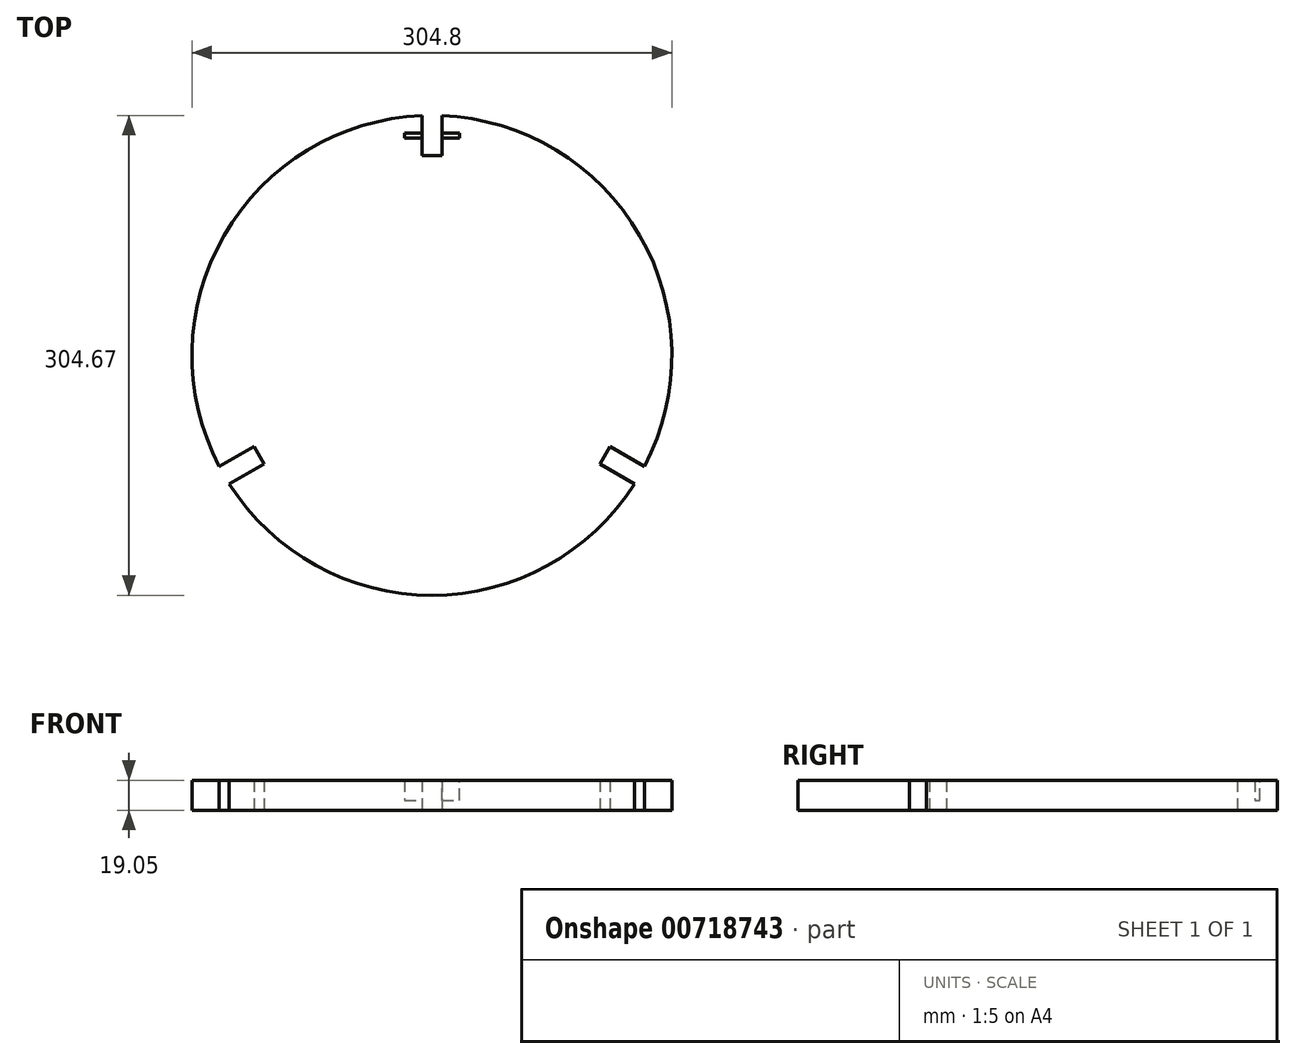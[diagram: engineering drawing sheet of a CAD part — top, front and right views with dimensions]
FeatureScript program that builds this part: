
annotation { "Feature Type Name" : "Feature", "Feature Type Description" : "" }
export const myFeature = defineFeature(function(context is Context, id is Id, definition is map)
    precondition{}
    {
        {
            var Q0;
            Q0=qCreatedBy(makeId("Top.planeOp"),FACE);
            var sketch = newSketch(context, id + "F0", { "sketchPlane" : qUnion([Q0])});
            skCircle(sketch, "E0", {"center": v(0, 0) * mm, "radius": 152.4 * mm});
            skLineSegment(sketch, "E1", {"start": v(0, 0) * mm, "end": v(0, 152.4) * mm, "construction": true});
            skLineSegment(sketch, "E2", {"start": v(0, 0) * mm, "end": v(131.98, -76.2) * mm, "construction": true});
            skLineSegment(sketch, "E3", {"start": v(0, 0) * mm, "end": v(-131.98, -76.2) * mm, "construction": true});
            skLineSegment(sketch, "E4", {"start": v(-6.35, 152.27) * mm, "end": v(-6.35, 126.87) * mm});
            skLineSegment(sketch, "E5", {"start": v(-6.35, 126.87) * mm, "end": v(6.35, 126.87) * mm});
            skLineSegment(sketch, "E6", {"start": v(6.35, 126.87) * mm, "end": v(6.35, 152.27) * mm});
            skLineSegment(sketch, "E7.1.0", {"start": v(-128.7, -81.63) * mm, "end": v(-106.7, -68.93) * mm});
            skLineSegment(sketch, "E7.1.1", {"start": v(-106.7, -68.93) * mm, "end": v(-113.05, -57.93) * mm});
            skLineSegment(sketch, "E7.1.2", {"start": v(-113.05, -57.93) * mm, "end": v(-135.04, -70.63) * mm});
            skLineSegment(sketch, "E7.2.0", {"start": v(135.04, -70.63) * mm, "end": v(113.05, -57.93) * mm});
            skLineSegment(sketch, "E7.2.1", {"start": v(113.05, -57.93) * mm, "end": v(106.7, -68.93) * mm});
            skLineSegment(sketch, "E7.2.2", {"start": v(106.7, -68.93) * mm, "end": v(128.7, -81.63) * mm});
            skSolve(sketch);
        }
        {
            var Q0;
            {var subQ0=sQuery(id+"F0.wireOp",EDGE,"E4");Q0=makeQuery(id+"F0.imprint","IMPRINT",FACE,{"disambiguationData":[TD([[makeQuery(id+"F0.imprint","IMPRINT",EDGE,{"derivedFrom":subQ0}),-1.0]])]});}
            extrude(context, id + "F1", {"entities" : qUnion([Q0]), "depth" : 19.05 * mm, "offsetDistance" : 25.4 * mm});
        }
        {
            var Q0;
            Q0=qCreatedBy(makeId("Right.planeOp"),FACE);
            var sketch = newSketch(context, id + "F2", { "sketchPlane" : qUnion([Q0])});
            skLineSegment(sketch, "E8.0.1", {"start": v(126.87, 0) * mm, "end": v(126.87, 19.05) * mm});
            skLineSegment(sketch, "E8.0.3", {"start": v(126.87, 19.05) * mm, "end": v(126.87, 0) * mm, "construction": true});
            skLineSegment(sketch, "E9.0", {"start": v(152.27, 19.05) * mm, "end": v(-70.63, 19.05) * mm, "construction": true});
            skLineSegment(sketch, "E10", {"start": v(137.98, 19.05) * mm, "end": v(137.98, 6.35) * mm});
            skLineSegment(sketch, "E11", {"start": v(137.98, 6.35) * mm, "end": v(141.16, 6.35) * mm});
            skLineSegment(sketch, "E12", {"start": v(141.16, 6.35) * mm, "end": v(141.16, 19.05) * mm});
            skLineSegment(sketch, "E13", {"start": v(137.98, 19.05) * mm, "end": v(141.16, 19.05) * mm});
            skLineSegment(sketch, "E14", {"start": v(139.57, 19.05) * mm, "end": v(139.57, 6.35) * mm, "construction": true});
            skLineSegment(sketch, "E15.0", {"start": v(152.27, 0) * mm, "end": v(-70.63, 0) * mm, "construction": true});
            skSolve(sketch);
        }
        {
            var Q0;
            Q0 = qSketchRegion(id + "F2", true);
            extrude(context, id + "F3", {"entities" : qUnion([Q0]), "operationType" : NewBodyOperationType.REMOVE, "endBound" : BoundingType.SYMMETRIC, "oppositeDirection" : true, "depth" : 34.92 * mm, "offsetDistance" : 25.4 * mm, "hasSecondDirection" : true, "secondDirectionOppositeDirection" : false, "secondDirectionDepth" : 15.88 * mm});
        }
    });
